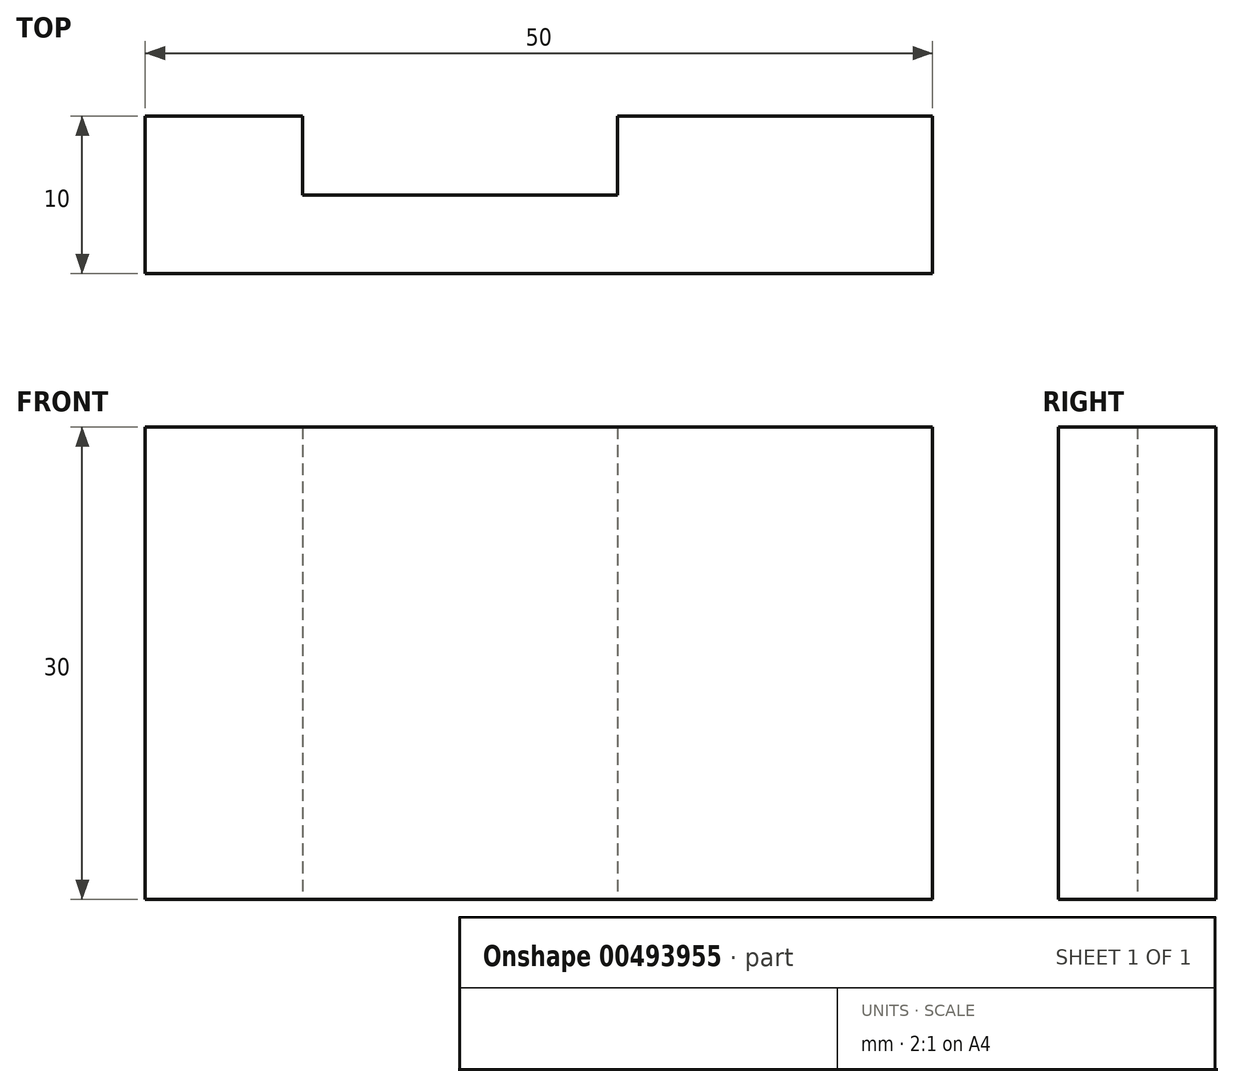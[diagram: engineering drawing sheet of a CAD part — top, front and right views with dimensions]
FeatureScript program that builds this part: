
annotation { "Feature Type Name" : "Feature", "Feature Type Description" : "" }
export const myFeature = defineFeature(function(context is Context, id is Id, definition is map)
    precondition{}
    {
        {
            var Q0;
            Q0=qCreatedBy(makeId("Top.planeOp"),FACE);
            var sketch = newSketch(context, id + "F0", { "sketchPlane" : qUnion([Q0])});
            skLineSegment(sketch, "E0", {"start": v(-35.5, 0) * mm, "end": v(-35.5, 10) * mm});
            skLineSegment(sketch, "E1", {"start": v(-35.5, 10) * mm, "end": v(-25.5, 10) * mm});
            skLineSegment(sketch, "E2", {"start": v(-25.5, 10) * mm, "end": v(-25.5, 5) * mm});
            skLineSegment(sketch, "E3", {"start": v(-25.5, 5) * mm, "end": v(-5.5, 5) * mm});
            skLineSegment(sketch, "E4", {"start": v(-5.5, 5) * mm, "end": v(-5.5, 10) * mm});
            skLineSegment(sketch, "E5", {"start": v(-35.5, 0) * mm, "end": v(14.5, 0) * mm});
            skLineSegment(sketch, "E6", {"start": v(-5.5, 10) * mm, "end": v(14.5, 10) * mm});
            skLineSegment(sketch, "E7", {"start": v(14.5, 10) * mm, "end": v(14.5, 0) * mm});
            skSolve(sketch);
        }
        {
            var Q0;
            Q0=makeQuery(id+"F0.imprint","IMPRINT",FACE,{"disambiguationData":[TD([[makeQuery(id+"F0.imprint","IMPRINT",EDGE,{"derivedFrom":sQuery(id+"F0.wireOp",EDGE,"E0")}),-1.0]])]});
            extrude(context, id + "F1", {"entities" : qUnion([Q0]), "depth" : 30 * mm});
        }
    });
